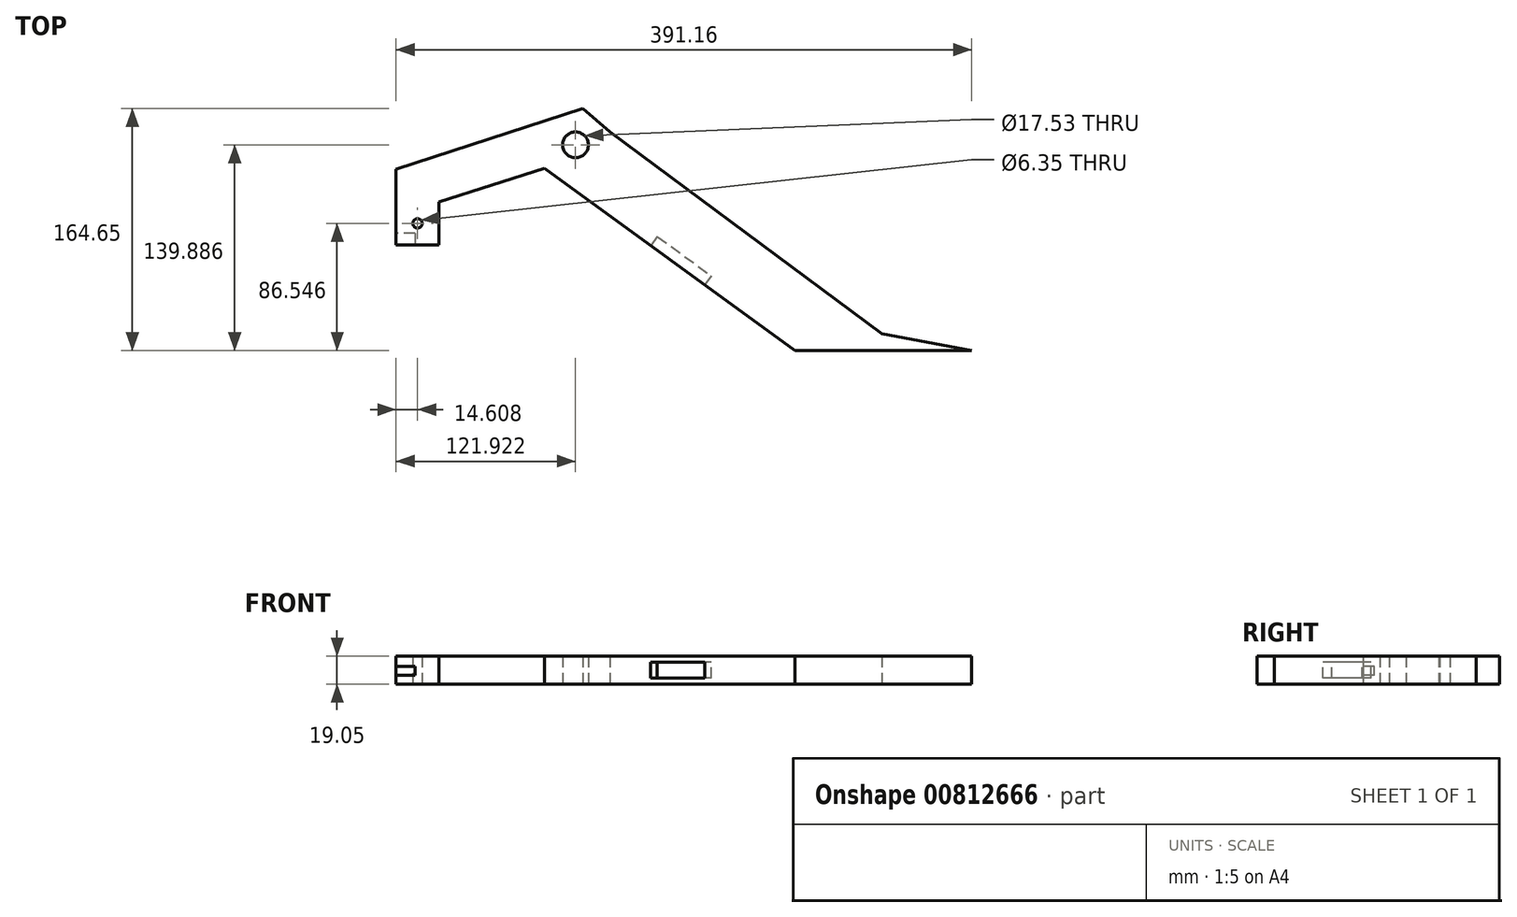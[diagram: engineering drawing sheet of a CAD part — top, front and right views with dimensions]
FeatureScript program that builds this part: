
annotation { "Feature Type Name" : "Feature", "Feature Type Description" : "" }
export const myFeature = defineFeature(function(context is Context, id is Id, definition is map)
    precondition{}
    {
        {
            var Q0;
            Q0=qCreatedBy(makeId("Top.planeOp"),FACE);
            var sketch = newSketch(context, id + "F0", { "sketchPlane" : qUnion([Q0])});
            skLineSegment(sketch, "E0", {"start": v(-7.58, 148.78) * mm, "end": v(177.2, 11.62) * mm});
            skLineSegment(sketch, "E1", {"start": v(177.2, 11.62) * mm, "end": v(238.16, 0) * mm});
            skLineSegment(sketch, "E2", {"start": v(118.15, 0) * mm, "end": v(-52.03, 124.01) * mm});
            skLineSegment(sketch, "E3", {"start": v(-52.03, 124.01) * mm, "end": v(-123.79, 101.15) * mm});
            skLineSegment(sketch, "E4", {"start": v(-123.79, 101.15) * mm, "end": v(-123.79, 71.94) * mm});
            skLineSegment(sketch, "E5", {"start": v(-123.79, 71.94) * mm, "end": v(-153, 71.94) * mm});
            skLineSegment(sketch, "E6", {"start": v(-153, 71.94) * mm, "end": v(-153, 123.38) * mm});
            skLineSegment(sketch, "E7", {"start": v(-153, 123.38) * mm, "end": v(-26, 164.65) * mm});
            skLineSegment(sketch, "E8", {"start": v(-26, 164.65) * mm, "end": v(-7.58, 148.78) * mm});
            skLineSegment(sketch, "E9", {"start": v(118.15, 0) * mm, "end": v(238.16, 0) * mm});
            skCircle(sketch, "E10", {"center": v(-31.08, 139.89) * mm, "radius": 8.77 * mm});
            skCircle(sketch, "E11", {"center": v(-138.4, 86.55) * mm, "radius": 3.17 * mm});
            skSolve(sketch);
        }
        {
            var Q0;
            Q0=makeQuery(id+"F0.imprint","IMPRINT",FACE,{"disambiguationData":[TD([[makeQuery(id+"F0.imprint","IMPRINT",EDGE,{"derivedFrom":sQuery(id+"F0.wireOp",EDGE,"E0")}),-1.0]])]});
            extrude(context, id + "F1", {"entities" : qUnion([Q0]), "depth" : 19.05 * mm, "offsetDistance" : 25.4 * mm});
        }
        {
            var Q0;
            Q0=makeQuery(id+"F1.opExtrude","SWEPT_FACE",FACE,{"disambiguationData":[OSD([sQuery(id+"F0.wireOp",EDGE,"E2")])]});
            var sketch = newSketch(context, id + "F2", { "sketchPlane" : qUnion([Q0])});
            skLineSegment(sketch, "E12.bottom", {"start": v(-25.9, 3.98) * mm, "end": v(19.58, 3.98) * mm});
            skLineSegment(sketch, "E12.top", {"start": v(-25.9, 15.07) * mm, "end": v(19.58, 15.07) * mm});
            skLineSegment(sketch, "E12.left", {"start": v(-25.9, 3.98) * mm, "end": v(-25.9, 15.07) * mm});
            skLineSegment(sketch, "E12.right", {"start": v(19.58, 3.98) * mm, "end": v(19.58, 15.07) * mm});
            skSolve(sketch);
        }
        {
            var Q0;
            Q0=makeQuery(id+"F2.imprint","IMPRINT",FACE,{"disambiguationData":[TD([[makeQuery(id+"F2.imprint","IMPRINT",EDGE,{"derivedFrom":sQuery(id+"F2.wireOp",EDGE,"E12.bottom")}),1.0]])]});
            extrude(context, id + "F3", {"entities" : qUnion([Q0]), "operationType" : NewBodyOperationType.REMOVE, "oppositeDirection" : true, "depth" : 7.62 * mm, "offsetDistance" : 25.4 * mm});
        }
        {
            var Q0;
            Q0=makeQuery(id+"F1.opExtrude","SWEPT_FACE",FACE,{"disambiguationData":[OSD([sQuery(id+"F0.wireOp",EDGE,"E6")])]});
            var sketch = newSketch(context, id + "F4", { "sketchPlane" : qUnion([Q0])});
            skLineSegment(sketch, "E13.bottom", {"start": v(-79.76, 6.06) * mm, "end": v(-71.94, 6.06) * mm});
            skLineSegment(sketch, "E13.top", {"start": v(-79.76, 11.91) * mm, "end": v(-71.94, 11.91) * mm});
            skLineSegment(sketch, "E13.left", {"start": v(-79.76, 6.06) * mm, "end": v(-79.76, 11.91) * mm});
            skLineSegment(sketch, "E13.right", {"start": v(-71.94, 6.06) * mm, "end": v(-71.94, 11.91) * mm});
            skSolve(sketch);
        }
        {
            var Q0;
            Q0 = qSketchRegion(id + "F4", true);
            extrude(context, id + "F5", {"entities" : qUnion([Q0]), "operationType" : NewBodyOperationType.REMOVE, "oppositeDirection" : true, "depth" : 12.95 * mm, "offsetDistance" : 25.4 * mm});
        }
    });
